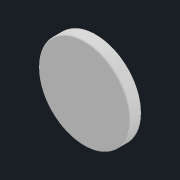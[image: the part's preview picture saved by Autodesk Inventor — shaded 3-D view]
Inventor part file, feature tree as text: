
AUTODESK INVENTOR PART (.ipt)
format: ipt  version: 2022.2 (Build 262287010, 287A)  size: 98,304 bytes
history: native  units: mm
features: extrude x1, fillet x1, sketch x1
ambient origin geometry x8: Origin, YZ Plane, XZ Plane, XY Plane, X Axis, Y Axis, Z Axis, Center Point
bodies: Solid1 (feature_tree)
feature tree (3):
  extrude  "Extrusion1"  Depth=2.0mm TaperAngle=0.0deg
  fillet  "Fillet1"  Radius=0.2mm
  sketch  "Sketch1"  dims[d0=15.0mm d1=2.0mm d2=0.0mm d3=0.2mm]
